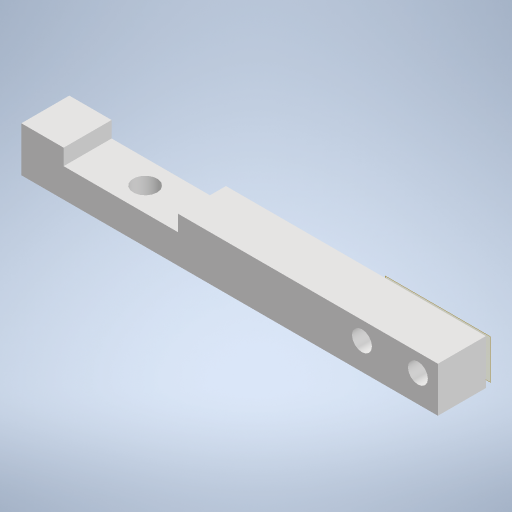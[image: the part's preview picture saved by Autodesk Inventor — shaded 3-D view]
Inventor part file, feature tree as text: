
AUTODESK INVENTOR PART (.ipt)
format: ipt  version: 2024.2 (Build 282272000, 272)  size: 232,448 bytes
history: native  units: mm
features: other x5, extrude x3, sketch x2, reference x1
ambient origin geometry x8: Origin, YZ Plane, XZ Plane, XY Plane, X Axis, Y Axis, Z Axis, Center Point
bodies: Body1 (feature_tree)
feature tree (11):
  other  "Твердое тело1"
  other  "РабПлоскость1"
  extrude  "Выдавливание1"  Depth=6.0mm TaperAngle=0.0deg
  sketch  "Эскиз2"
  extrude  "Выдавливание2"  Depth=3.0mm
  extrude  "Выдавливание3"  Depth=3.0mm
  sketch  "Эскиз1"
  reference  "Ссылка1"
  other  "<userpath>\Documents\Artist-v2\3D\каретка.iam"
  other  "каретка.iam"
  other  "Сервопривод:1"
